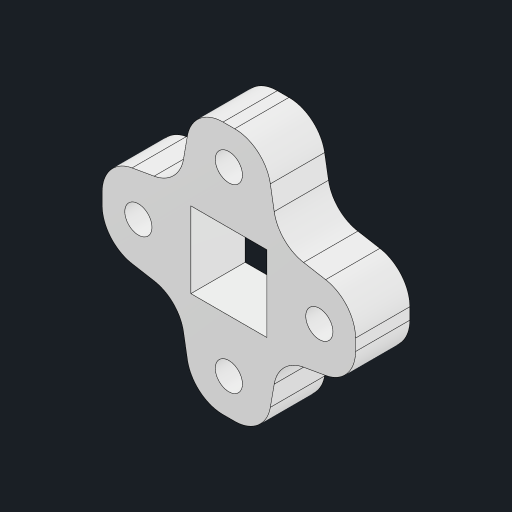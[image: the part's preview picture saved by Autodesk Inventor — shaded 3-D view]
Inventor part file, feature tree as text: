
AUTODESK INVENTOR PART (.ipt)
format: ipt  version: 2023 (Build 270158000, 158)  size: 166,912 bytes
history: native  units: mm
features: other x1, extrude x1, fillet x1, sketch x1
ambient origin geometry x8: Origin, YZ Plane, XZ Plane, XY Plane, X Axis, Y Axis, Z Axis, Center Point
bodies: Body1 (feature_tree)
feature tree (4):
  other  "ソリッド1"
  extrude  "押し出し1"  Depth=3.0mm TaperAngle=0.0deg
  fillet  "フィレット1"  Radius=4.0mm
  sketch  "スケッチ1"
